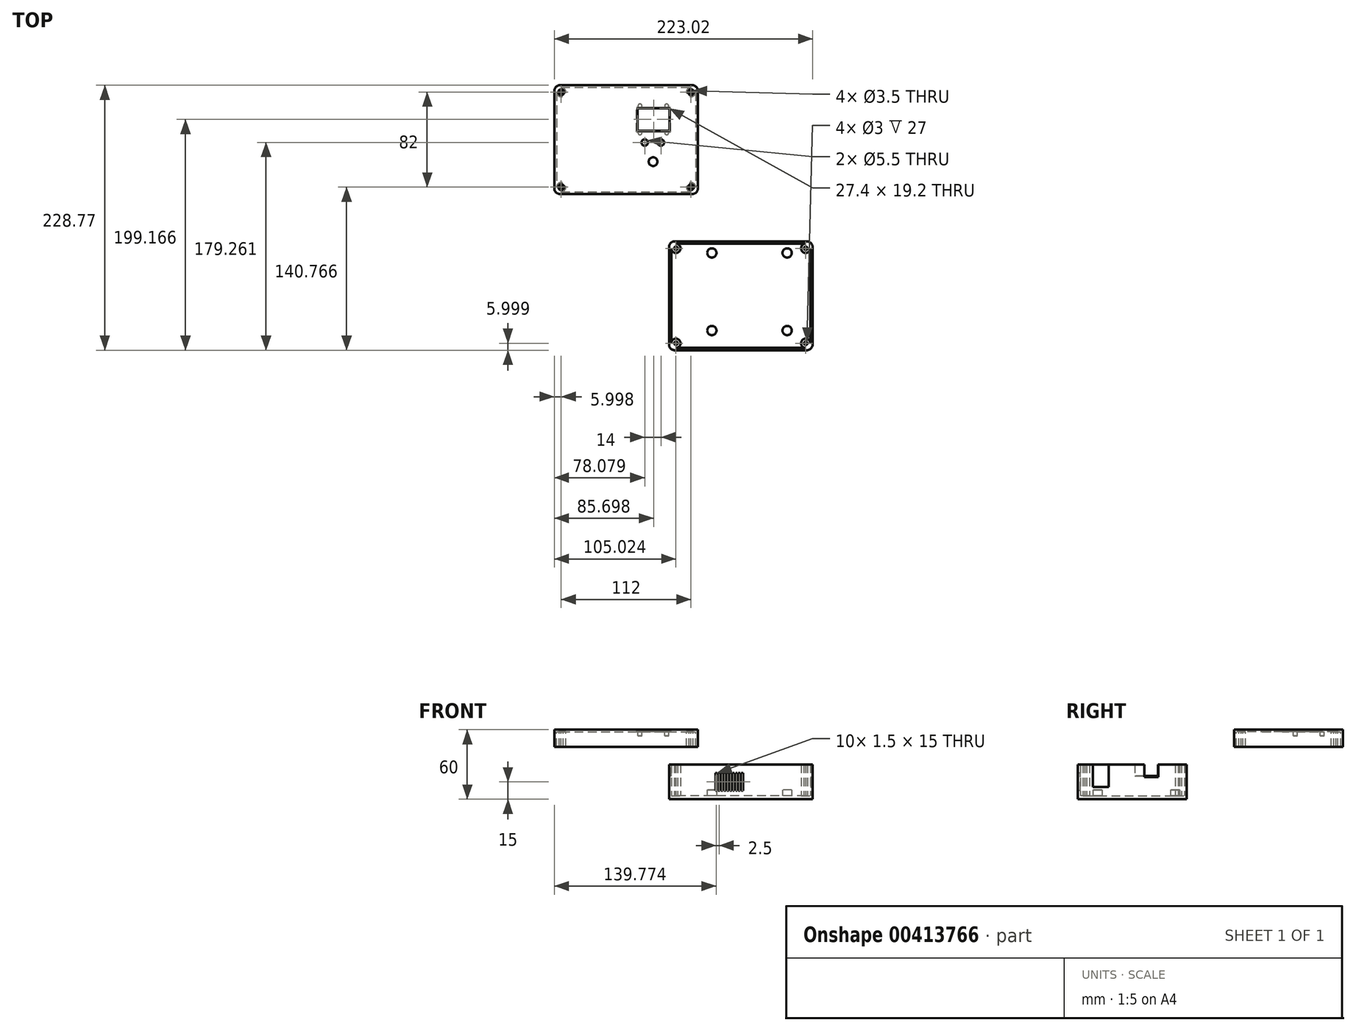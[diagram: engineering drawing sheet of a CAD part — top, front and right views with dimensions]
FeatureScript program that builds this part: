
annotation { "Feature Type Name" : "Feature", "Feature Type Description" : "" }
export const myFeature = defineFeature(function(context is Context, id is Id, definition is map)
    precondition{}
    {
        {
            var Q0;
            Q0=qCreatedBy(makeId("Top.planeOp"),FACE);
            var sketch = newSketch(context, id + "F0", { "sketchPlane" : qUnion([Q0])});
            skLineSegment(sketch, "E0.bottom", {"start": v(-58.78, 54.64) * mm, "end": v(53.22, 54.64) * mm});
            skLineSegment(sketch, "E0.top", {"start": v(-58.78, -35.36) * mm, "end": v(53.22, -35.36) * mm});
            skLineSegment(sketch, "E0.left", {"start": v(-62.78, 50.64) * mm, "end": v(-62.78, -31.36) * mm});
            skLineSegment(sketch, "E0.right", {"start": v(57.22, 50.64) * mm, "end": v(57.22, -31.36) * mm});
            skCircle(sketch, "E1", {"center": v(-58.78, 50.64) * mm, "radius": 4 * mm});
            skCircle(sketch, "E2", {"center": v(53.22, 50.64) * mm, "radius": 4 * mm});
            skCircle(sketch, "E3", {"center": v(-58.78, -31.36) * mm, "radius": 4 * mm});
            skCircle(sketch, "E4", {"center": v(53.22, -31.36) * mm, "radius": 4 * mm});
            skCircle(sketch, "E5", {"center": v(-58.78, 50.64) * mm, "radius": 1.5 * mm});
            skCircle(sketch, "E6", {"center": v(-58.78, -31.36) * mm, "radius": 1.5 * mm});
            skCircle(sketch, "E7", {"center": v(53.22, -31.36) * mm, "radius": 1.5 * mm});
            skCircle(sketch, "E8", {"center": v(53.22, 50.64) * mm, "radius": 1.5 * mm});
            skLineSegment(sketch, "E9.0", {"start": v(-64.78, 56.64) * mm, "end": v(59.22, 56.64) * mm});
            skLineSegment(sketch, "E9.1", {"start": v(-64.78, 56.64) * mm, "end": v(-64.78, -37.36) * mm});
            skLineSegment(sketch, "E9.2", {"start": v(-64.78, -37.36) * mm, "end": v(59.22, -37.36) * mm});
            skLineSegment(sketch, "E9.3", {"start": v(59.22, 56.64) * mm, "end": v(59.22, -37.36) * mm});
            skPoint(sketch, "E10.visualSharp", {"position": v(-62.78, 54.64) * mm});
            skArc(sketch, "E10.filletArc", {"start": v(-58.78, 54.64) * mm, "mid": v(-61.6, 53.47) * mm, "end": v(-62.78, 50.64) * mm});
            skPoint(sketch, "E11.visualSharp", {"position": v(57.22, 54.64) * mm});
            skArc(sketch, "E11.filletArc", {"start": v(57.22, 50.64) * mm, "mid": v(56.05, 53.47) * mm, "end": v(53.22, 54.64) * mm});
            skPoint(sketch, "E12.visualSharp", {"position": v(57.22, -35.36) * mm});
            skArc(sketch, "E12.filletArc", {"start": v(53.22, -35.36) * mm, "mid": v(56.05, -34.19) * mm, "end": v(57.22, -31.36) * mm});
            skPoint(sketch, "E13.visualSharp", {"position": v(-62.78, -35.36) * mm});
            skArc(sketch, "E13.filletArc", {"start": v(-62.78, -31.36) * mm, "mid": v(-61.6, -34.19) * mm, "end": v(-58.78, -35.36) * mm});
            skSolve(sketch);
        }
        {
            var Q0;
            Q0=makeQuery(id+"F0.imprint","IMPRINT",FACE,{"disambiguationData":[TD([[makeQuery(id+"F0.imprint","IMPRINT",EDGE,{"derivedFrom":sQuery(id+"F0.wireOp",EDGE,"E5")}),-1.0]])]});
            var Q1;
            Q1=makeQuery(id+"F0.imprint","IMPRINT",FACE,{"disambiguationData":[TD([[makeQuery(id+"F0.imprint","IMPRINT",EDGE,{"derivedFrom":sQuery(id+"F0.wireOp",EDGE,"E7")}),-1.0]])]});
            var Q2;
            Q2=makeQuery(id+"F0.imprint","IMPRINT",FACE,{"disambiguationData":[TD([[makeQuery(id+"F0.imprint","IMPRINT",EDGE,{"derivedFrom":sQuery(id+"F0.wireOp",EDGE,"E8")}),-1.0]])]});
            var Q3;
            Q3=makeQuery(id+"F0.imprint","IMPRINT",FACE,{"disambiguationData":[TD([[makeQuery(id+"F0.imprint","IMPRINT",EDGE,{"derivedFrom":sQuery(id+"F0.wireOp",EDGE,"E6")}),-1.0]])]});
            var Q4;
            {var subQ3=sQuery(id+"F0.wireOp",EDGE,"E0.bottom");Q4=makeQuery(id+"F0.imprint","IMPRINT",FACE,{"disambiguationData":[TD([[makeQuery(id+"F0.imprint","IMPRINT",EDGE,{"derivedFrom":subQ3}),-1.0]])]});}
            var Q5;
            {var subQ4=sQuery(id+"F0.wireOp",EDGE,"E0.bottom");Q5=makeQuery(id+"F0.imprint","IMPRINT",FACE,{"disambiguationData":[TD([[makeQuery(id+"F0.imprint","IMPRINT",EDGE,{"derivedFrom":subQ4}),1.0]])]});}
            var Q6;
            Q6=makeQuery(id+"F0.imprint","IMPRINT",FACE,{"disambiguationData":[TD([[makeQuery(id+"F0.imprint","IMPRINT",EDGE,{"derivedFrom":sQuery(id+"F0.wireOp",EDGE,"E7")}),1.0]])]});
            var Q7;
            Q7=makeQuery(id+"F0.imprint","IMPRINT",FACE,{"disambiguationData":[TD([[makeQuery(id+"F0.imprint","IMPRINT",EDGE,{"derivedFrom":sQuery(id+"F0.wireOp",EDGE,"E5")}),1.0]])]});
            var Q8;
            Q8=makeQuery(id+"F0.imprint","IMPRINT",FACE,{"disambiguationData":[TD([[makeQuery(id+"F0.imprint","IMPRINT",EDGE,{"derivedFrom":sQuery(id+"F0.wireOp",EDGE,"E8")}),1.0]])]});
            var Q9;
            Q9=makeQuery(id+"F0.imprint","IMPRINT",FACE,{"disambiguationData":[TD([[makeQuery(id+"F0.imprint","IMPRINT",EDGE,{"derivedFrom":sQuery(id+"F0.wireOp",EDGE,"E6")}),1.0]])]});
            extrude(context, id + "F1", {"entities" : qUnion([Q0, Q1, Q2, Q3, Q4, Q5, Q6, Q7, Q8, Q9]), "offsetDistance" : 25 * mm, "depth" : 3 * mm});
        }
        {
            var Q0;
            Q0=makeQuery(id+"F0.imprint","IMPRINT",FACE,{"disambiguationData":[TD([[makeQuery(id+"F0.imprint","IMPRINT",EDGE,{"derivedFrom":sQuery(id+"F0.wireOp",EDGE,"E5")}),-1.0]])]});
            var Q1;
            Q1=makeQuery(id+"F0.imprint","IMPRINT",FACE,{"disambiguationData":[TD([[makeQuery(id+"F0.imprint","IMPRINT",EDGE,{"derivedFrom":sQuery(id+"F0.wireOp",EDGE,"E8")}),-1.0]])]});
            var Q2;
            Q2=makeQuery(id+"F0.imprint","IMPRINT",FACE,{"disambiguationData":[TD([[makeQuery(id+"F0.imprint","IMPRINT",EDGE,{"derivedFrom":sQuery(id+"F0.wireOp",EDGE,"E7")}),-1.0]])]});
            var Q3;
            Q3=makeQuery(id+"F0.imprint","IMPRINT",FACE,{"disambiguationData":[TD([[makeQuery(id+"F0.imprint","IMPRINT",EDGE,{"derivedFrom":sQuery(id+"F0.wireOp",EDGE,"E6")}),-1.0]])]});
            var Q4;
            {var subQ4=sQuery(id+"F0.wireOp",EDGE,"E0.bottom");Q4=makeQuery(id+"F0.imprint","IMPRINT",FACE,{"disambiguationData":[TD([[makeQuery(id+"F0.imprint","IMPRINT",EDGE,{"derivedFrom":subQ4}),1.0]])]});}
            extrude(context, id + "F2", {"entities" : qUnion([Q0, Q1, Q2, Q3, Q4]), "operationType" : NewBodyOperationType.ADD, "depth" : 30 * mm});
        }
        {
            var Q0;
            {var subQ0=sQuery(id+"F0.wireOp",EDGE,"E9.1");var subQ1=sQuery(id+"F0.wireOp",EDGE,"E9.0");Q0=makeQuery(id+"F2.boolean.opBoolean","MERGE",EDGE,{"derivedFrom":[makeQuery(id+"F1.opExtrude","SWEPT_EDGE",EDGE,{"disambiguationData":[OSD([subQ1,subQ0])]}),makeQuery(id+"F2.opExtrude","SWEPT_EDGE",EDGE,{"disambiguationData":[OSD([subQ1,subQ0])]})]});}
            var Q1;
            {var subQ0=sQuery(id+"F0.wireOp",EDGE,"E9.3");var subQ1=sQuery(id+"F0.wireOp",EDGE,"E9.0");Q1=makeQuery(id+"F2.boolean.opBoolean","MERGE",EDGE,{"derivedFrom":[makeQuery(id+"F1.opExtrude","SWEPT_EDGE",EDGE,{"disambiguationData":[OSD([subQ1,subQ0])]}),makeQuery(id+"F2.opExtrude","SWEPT_EDGE",EDGE,{"disambiguationData":[OSD([subQ1,subQ0])]})]});}
            var Q2;
            {var subQ0=sQuery(id+"F0.wireOp",EDGE,"E9.3");var subQ1=sQuery(id+"F0.wireOp",EDGE,"E9.2");Q2=makeQuery(id+"F2.boolean.opBoolean","MERGE",EDGE,{"derivedFrom":[makeQuery(id+"F1.opExtrude","SWEPT_EDGE",EDGE,{"disambiguationData":[OSD([subQ1,subQ0])]}),makeQuery(id+"F2.opExtrude","SWEPT_EDGE",EDGE,{"disambiguationData":[OSD([subQ1,subQ0])]})]});}
            var Q3;
            {var subQ0=sQuery(id+"F0.wireOp",EDGE,"E9.2");var subQ1=sQuery(id+"F0.wireOp",EDGE,"E9.1");Q3=makeQuery(id+"F2.boolean.opBoolean","MERGE",EDGE,{"derivedFrom":[makeQuery(id+"F1.opExtrude","SWEPT_EDGE",EDGE,{"disambiguationData":[OSD([subQ1,subQ0])]}),makeQuery(id+"F2.opExtrude","SWEPT_EDGE",EDGE,{"disambiguationData":[OSD([subQ1,subQ0])]})]});}
            fillet(context, id + "F3", {"entities" : qUnion([Q0, Q1, Q2, Q3]), "radius" : 5 * mm, "tangentPropagation" : true, "allowEdgeOverflow" : false});
        }
        {
            var Q0;
            Q0=makeQuery(id+"F2.boolean.opBoolean","SPLIT",FACE,{"disambiguationData":[TD([makeQuery(id+"F2.opExtrude","SWEPT_FACE",FACE,{"disambiguationData":[OSD([sQuery(id+"F0.wireOp",EDGE,"E0.bottom")])]})])],"derivedFrom":makeQuery(id+"F1.opExtrude","CAP_FACE",FACE,{"disambiguationData":[OSD([sQuery(id+"F0.wireOp",EDGE,"E9.0"),sQuery(id+"F0.wireOp",EDGE,"E9.1"),sQuery(id+"F0.wireOp",EDGE,"E9.2"),sQuery(id+"F0.wireOp",EDGE,"E9.3")])],"isStart":false})});
            var sketch = newSketch(context, id + "F4", { "sketchPlane" : qUnion([Q0])});
            skCircle(sketch, "E14", {"center": v(-27.78, 46.64) * mm, "radius": 4 * mm});
            skCircle(sketch, "E15", {"center": v(37.22, 46.64) * mm, "radius": 4 * mm});
            skCircle(sketch, "E16", {"center": v(-27.78, -20.36) * mm, "radius": 4 * mm});
            skCircle(sketch, "E17", {"center": v(37.22, -20.36) * mm, "radius": 4 * mm});
            skSolve(sketch);
        }
        {
            var Q0;
            Q0 = qSketchRegion(id + "F4", true);
            extrude(context, id + "F5", {"entities" : qUnion([Q0]), "operationType" : NewBodyOperationType.ADD, "offsetDistance" : 25 * mm, "depth" : 5 * mm});
        }
        {
            var Q0;
            {var subQ0=sQuery(id+"F0.wireOp",EDGE,"E9.3");Q0=makeQuery(id+"F2.boolean.opBoolean","MERGE",FACE,{"derivedFrom":[makeQuery(id+"F1.opExtrude","SWEPT_FACE",FACE,{"disambiguationData":[OSD([subQ0])]}),makeQuery(id+"F2.opExtrude","SWEPT_FACE",FACE,{"disambiguationData":[OSD([subQ0])]})]});}
            var sketch = newSketch(context, id + "F6", { "sketchPlane" : qUnion([Q0])});
            skLineSegment(sketch, "E18.bottom", {"start": v(-24.36, 30) * mm, "end": v(-10.86, 30) * mm});
            skLineSegment(sketch, "E18.top", {"start": v(-24.36, 10.5) * mm, "end": v(-10.86, 10.5) * mm});
            skLineSegment(sketch, "E18.left", {"start": v(-24.36, 30) * mm, "end": v(-24.36, 10.5) * mm});
            skLineSegment(sketch, "E18.right", {"start": v(-10.86, 30) * mm, "end": v(-10.86, 10.5) * mm});
            skLineSegment(sketch, "E19.bottom", {"start": v(20.14, 30) * mm, "end": v(32.14, 30) * mm});
            skLineSegment(sketch, "E19.top", {"start": v(20.14, 19) * mm, "end": v(32.14, 19) * mm});
            skLineSegment(sketch, "E19.left", {"start": v(20.14, 30) * mm, "end": v(20.14, 19) * mm});
            skLineSegment(sketch, "E19.right", {"start": v(32.14, 30) * mm, "end": v(32.14, 19) * mm});
            skSolve(sketch);
        }
        {
            var Q0;
            Q0 = qSketchRegion(id + "F6", true);
            extrude(context, id + "F7", {"entities" : qUnion([Q0]), "operationType" : NewBodyOperationType.REMOVE, "oppositeDirection" : true, "depth" : 3 * mm});
        }
        {
            var Q0;
            {var subQ0=sQuery(id+"F0.wireOp",EDGE,"E9.1");Q0=makeQuery(id+"F2.boolean.opBoolean","MERGE",FACE,{"derivedFrom":[makeQuery(id+"F1.opExtrude","SWEPT_FACE",FACE,{"disambiguationData":[OSD([subQ0])]}),makeQuery(id+"F2.opExtrude","SWEPT_FACE",FACE,{"disambiguationData":[OSD([subQ0])]})]});}
            var sketch = newSketch(context, id + "F8", { "sketchPlane" : qUnion([Q0])});
            skLineSegment(sketch, "E20.bottom", {"start": v(-31.64, 30) * mm, "end": v(-11.64, 30) * mm});
            skLineSegment(sketch, "E20.top", {"start": v(-31.64, 20) * mm, "end": v(-11.64, 20) * mm});
            skLineSegment(sketch, "E20.left", {"start": v(-31.64, 30) * mm, "end": v(-31.64, 20) * mm});
            skLineSegment(sketch, "E20.right", {"start": v(-11.64, 30) * mm, "end": v(-11.64, 20) * mm});
            skSolve(sketch);
        }
        {
            var Q0;
            Q0=qCreatedBy(makeId("Top.planeOp"),FACE);
            cPlane(context, id + "F9", {"entities" : qUnion([Q0]), "cplaneType" : CPlaneType.OFFSET, "offset" : 60 * mm, "width" : 150 * mm, "height" : 150 * mm});
        }
        {
            var Q0;
            Q0=qCreatedBy(id+"F9.planeOp",FACE);
            var sketch = newSketch(context, id + "F10", { "sketchPlane" : qUnion([Q0])});
            skLineSegment(sketch, "E21.bottom", {"start": v(-157.8, 189.4) * mm, "end": v(-45.8, 189.4) * mm});
            skLineSegment(sketch, "E21.top", {"start": v(-157.8, 99.4) * mm, "end": v(-45.8, 99.4) * mm});
            skLineSegment(sketch, "E21.left", {"start": v(-161.8, 185.4) * mm, "end": v(-161.8, 103.4) * mm});
            skLineSegment(sketch, "E21.right", {"start": v(-41.8, 185.4) * mm, "end": v(-41.8, 103.4) * mm});
            skCircle(sketch, "E22", {"center": v(-157.8, 185.4) * mm, "radius": 4 * mm});
            skCircle(sketch, "E23", {"center": v(-45.8, 185.4) * mm, "radius": 4 * mm});
            skCircle(sketch, "E24", {"center": v(-157.8, 103.4) * mm, "radius": 4 * mm});
            skCircle(sketch, "E25", {"center": v(-45.8, 103.4) * mm, "radius": 4 * mm});
            skCircle(sketch, "E26", {"center": v(-157.8, 185.4) * mm, "radius": 1.5 * mm});
            skCircle(sketch, "E27", {"center": v(-157.8, 103.4) * mm, "radius": 1.5 * mm});
            skCircle(sketch, "E28", {"center": v(-45.8, 103.4) * mm, "radius": 1.5 * mm});
            skCircle(sketch, "E29", {"center": v(-45.8, 185.4) * mm, "radius": 1.5 * mm});
            skLineSegment(sketch, "E30.0", {"start": v(-163.8, 191.4) * mm, "end": v(-39.8, 191.4) * mm});
            skLineSegment(sketch, "E30.1", {"start": v(-163.8, 191.4) * mm, "end": v(-163.8, 97.4) * mm});
            skLineSegment(sketch, "E30.2", {"start": v(-163.8, 97.4) * mm, "end": v(-39.8, 97.4) * mm});
            skLineSegment(sketch, "E30.3", {"start": v(-39.8, 191.4) * mm, "end": v(-39.8, 97.4) * mm});
            skPoint(sketch, "E31.visualSharp", {"position": v(-161.8, 189.4) * mm});
            skArc(sketch, "E31.filletArc", {"start": v(-157.8, 189.4) * mm, "mid": v(-160.63, 188.23) * mm, "end": v(-161.8, 185.4) * mm});
            skPoint(sketch, "E32.visualSharp", {"position": v(-41.8, 189.4) * mm});
            skArc(sketch, "E32.filletArc", {"start": v(-41.8, 185.4) * mm, "mid": v(-42.97, 188.23) * mm, "end": v(-45.8, 189.4) * mm});
            skPoint(sketch, "E33.visualSharp", {"position": v(-41.8, 99.4) * mm});
            skArc(sketch, "E33.filletArc", {"start": v(-45.8, 99.4) * mm, "mid": v(-42.97, 100.58) * mm, "end": v(-41.8, 103.4) * mm});
            skPoint(sketch, "E34.visualSharp", {"position": v(-161.8, 99.4) * mm});
            skArc(sketch, "E34.filletArc", {"start": v(-161.8, 103.4) * mm, "mid": v(-160.63, 100.58) * mm, "end": v(-157.8, 99.4) * mm});
            skSolve(sketch);
        }
        {
            var Q0;
            {var subQ3=sQuery(id+"F10.wireOp",EDGE,"E21.bottom");Q0=makeQuery(id+"F10.imprint","IMPRINT",FACE,{"disambiguationData":[TD([[makeQuery(id+"F10.imprint","IMPRINT",EDGE,{"derivedFrom":subQ3}),-1.0]])]});}
            var Q1;
            {var subQ4=sQuery(id+"F10.wireOp",EDGE,"E21.bottom");Q1=makeQuery(id+"F10.imprint","IMPRINT",FACE,{"disambiguationData":[TD([[makeQuery(id+"F10.imprint","IMPRINT",EDGE,{"derivedFrom":subQ4}),1.0]])]});}
            var Q2;
            Q2=makeQuery(id+"F10.imprint","IMPRINT",FACE,{"disambiguationData":[TD([[makeQuery(id+"F10.imprint","IMPRINT",EDGE,{"derivedFrom":sQuery(id+"F10.wireOp",EDGE,"E26")}),-1.0]])]});
            var Q3;
            Q3=makeQuery(id+"F10.imprint","IMPRINT",FACE,{"disambiguationData":[TD([[makeQuery(id+"F10.imprint","IMPRINT",EDGE,{"derivedFrom":sQuery(id+"F10.wireOp",EDGE,"E29")}),-1.0]])]});
            var Q4;
            Q4=makeQuery(id+"F10.imprint","IMPRINT",FACE,{"disambiguationData":[TD([[makeQuery(id+"F10.imprint","IMPRINT",EDGE,{"derivedFrom":sQuery(id+"F10.wireOp",EDGE,"E28")}),-1.0]])]});
            var Q5;
            Q5=makeQuery(id+"F10.imprint","IMPRINT",FACE,{"disambiguationData":[TD([[makeQuery(id+"F10.imprint","IMPRINT",EDGE,{"derivedFrom":sQuery(id+"F10.wireOp",EDGE,"E27")}),-1.0]])]});
            extrude(context, id + "F11", {"entities" : qUnion([Q0, Q1, Q2, Q3, Q4, Q5]), "oppositeDirection" : true, "depth" : 2 * mm});
        }
        {
            var Q0;
            {var subQ4=sQuery(id+"F10.wireOp",EDGE,"E21.bottom");Q0=makeQuery(id+"F10.imprint","IMPRINT",FACE,{"disambiguationData":[TD([[makeQuery(id+"F10.imprint","IMPRINT",EDGE,{"derivedFrom":subQ4}),1.0]])]});}
            var Q1;
            Q1=makeQuery(id+"F10.imprint","IMPRINT",FACE,{"disambiguationData":[TD([[makeQuery(id+"F10.imprint","IMPRINT",EDGE,{"derivedFrom":sQuery(id+"F10.wireOp",EDGE,"E26")}),-1.0]])]});
            var Q2;
            Q2=makeQuery(id+"F10.imprint","IMPRINT",FACE,{"disambiguationData":[TD([[makeQuery(id+"F10.imprint","IMPRINT",EDGE,{"derivedFrom":sQuery(id+"F10.wireOp",EDGE,"E29")}),-1.0]])]});
            var Q3;
            Q3=makeQuery(id+"F10.imprint","IMPRINT",FACE,{"disambiguationData":[TD([[makeQuery(id+"F10.imprint","IMPRINT",EDGE,{"derivedFrom":sQuery(id+"F10.wireOp",EDGE,"E28")}),-1.0]])]});
            var Q4;
            Q4=makeQuery(id+"F10.imprint","IMPRINT",FACE,{"disambiguationData":[TD([[makeQuery(id+"F10.imprint","IMPRINT",EDGE,{"derivedFrom":sQuery(id+"F10.wireOp",EDGE,"E27")}),-1.0]])]});
            extrude(context, id + "F12", {"entities" : qUnion([Q0, Q1, Q2, Q3, Q4]), "operationType" : NewBodyOperationType.ADD, "oppositeDirection" : true, "depth" : 15 * mm});
        }
        {
            var Q0;
            {var subQ0=sQuery(id+"F10.wireOp",EDGE,"E30.1");var subQ1=sQuery(id+"F10.wireOp",EDGE,"E30.0");Q0=makeQuery(id+"F12.boolean.opBoolean","MERGE",EDGE,{"derivedFrom":[makeQuery(id+"F11.opExtrude","SWEPT_EDGE",EDGE,{"disambiguationData":[OSD([subQ1,subQ0])]}),makeQuery(id+"F12.opExtrude","SWEPT_EDGE",EDGE,{"disambiguationData":[OSD([subQ1,subQ0])]})]});}
            var Q1;
            {var subQ0=sQuery(id+"F10.wireOp",EDGE,"E30.3");var subQ1=sQuery(id+"F10.wireOp",EDGE,"E30.0");Q1=makeQuery(id+"F12.boolean.opBoolean","MERGE",EDGE,{"derivedFrom":[makeQuery(id+"F11.opExtrude","SWEPT_EDGE",EDGE,{"disambiguationData":[OSD([subQ1,subQ0])]}),makeQuery(id+"F12.opExtrude","SWEPT_EDGE",EDGE,{"disambiguationData":[OSD([subQ1,subQ0])]})]});}
            var Q2;
            {var subQ0=sQuery(id+"F10.wireOp",EDGE,"E30.3");var subQ1=sQuery(id+"F10.wireOp",EDGE,"E30.2");Q2=makeQuery(id+"F12.boolean.opBoolean","MERGE",EDGE,{"derivedFrom":[makeQuery(id+"F11.opExtrude","SWEPT_EDGE",EDGE,{"disambiguationData":[OSD([subQ1,subQ0])]}),makeQuery(id+"F12.opExtrude","SWEPT_EDGE",EDGE,{"disambiguationData":[OSD([subQ1,subQ0])]})]});}
            var Q3;
            {var subQ0=sQuery(id+"F10.wireOp",EDGE,"E30.2");var subQ1=sQuery(id+"F10.wireOp",EDGE,"E30.1");Q3=makeQuery(id+"F12.boolean.opBoolean","MERGE",EDGE,{"derivedFrom":[makeQuery(id+"F11.opExtrude","SWEPT_EDGE",EDGE,{"disambiguationData":[OSD([subQ1,subQ0])]}),makeQuery(id+"F12.opExtrude","SWEPT_EDGE",EDGE,{"disambiguationData":[OSD([subQ1,subQ0])]})]});}
            fillet(context, id + "F13", {"entities" : qUnion([Q0, Q1, Q2, Q3]), "radius" : 5 * mm, "tangentPropagation" : true, "allowEdgeOverflow" : false});
        }
        {
            var Q0;
            Q0=makeQuery(id+"F11.opExtrude","CAP_FACE",FACE,{"disambiguationData":[OSD([sQuery(id+"F10.wireOp",EDGE,"E26"),sQuery(id+"F10.wireOp",EDGE,"E27"),sQuery(id+"F10.wireOp",EDGE,"E28"),sQuery(id+"F10.wireOp",EDGE,"E29"),sQuery(id+"F10.wireOp",EDGE,"E30.0"),sQuery(id+"F10.wireOp",EDGE,"E30.1"),sQuery(id+"F10.wireOp",EDGE,"E30.2"),sQuery(id+"F10.wireOp",EDGE,"E30.3")])],"isStart":false});
            var sketch = newSketch(context, id + "F14", { "sketchPlane" : qUnion([Q0])});
            skCircle(sketch, "E35", {"center": v(-66.8, -173.4) * mm, "radius": 1.75 * mm});
            skCircle(sketch, "E36", {"center": v(-89.8, -173.4) * mm, "radius": 1.75 * mm});
            skCircle(sketch, "E37", {"center": v(-89.8, -150.4) * mm, "radius": 1.75 * mm});
            skCircle(sketch, "E38", {"center": v(-66.8, -150.4) * mm, "radius": 1.75 * mm});
            skSolve(sketch);
        }
        {
            var Q0;
            Q0=qCreatedBy(id+"F9.planeOp",FACE);
            var sketch = newSketch(context, id + "F15", { "sketchPlane" : qUnion([Q0])});
            skLineSegment(sketch, "E39.bottom", {"start": v(-91.8, 171.4) * mm, "end": v(-64.4, 171.4) * mm});
            skLineSegment(sketch, "E39.top", {"start": v(-91.8, 152.2) * mm, "end": v(-64.4, 152.2) * mm});
            skLineSegment(sketch, "E39.left", {"start": v(-91.8, 171.4) * mm, "end": v(-91.8, 152.2) * mm});
            skLineSegment(sketch, "E39.right", {"start": v(-64.4, 171.4) * mm, "end": v(-64.4, 152.2) * mm});
            skSolve(sketch);
        }
        {
            var Q0;
            Q0 = qSketchRegion(id + "F15", true);
            extrude(context, id + "F16", {"entities" : qUnion([Q0]), "operationType" : NewBodyOperationType.REMOVE, "oppositeDirection" : true, "offsetDistance" : 25 * mm, "depth" : 2 * mm});
        }
        {
            var Q0;
            Q0=makeQuery(id+"F14.imprint","IMPRINT",FACE,{"disambiguationData":[TD([[makeQuery(id+"F14.imprint","IMPRINT",EDGE,{"derivedFrom":sQuery(id+"F14.wireOp",EDGE,"E36")}),-1.0]])]});
            var sketch = newSketch(context, id + "F17", { "sketchPlane" : qUnion([Q0])});
            skLineSegment(sketch, "E40", {"start": v(-92.8, -141.12) * mm, "end": v(-92.8, -184.54) * mm, "construction": true});
            skLineSegment(sketch, "E41", {"start": v(-103.77, -151.2) * mm, "end": v(-49.87, -151.2) * mm, "construction": true});
            skLineSegment(sketch, "E42", {"start": v(-103.08, -172.4) * mm, "end": v(-49.67, -172.4) * mm, "construction": true});
            skLineSegment(sketch, "E43", {"start": v(-63.4, -142.01) * mm, "end": v(-63.4, -183.55) * mm, "construction": true});
            skLineSegment(sketch, "E44.bottom", {"start": v(-92.8, -151.2) * mm, "end": v(-63.4, -151.2) * mm});
            skLineSegment(sketch, "E44.top", {"start": v(-92.8, -172.4) * mm, "end": v(-63.4, -172.4) * mm});
            skLineSegment(sketch, "E44.left", {"start": v(-92.8, -151.2) * mm, "end": v(-92.8, -172.4) * mm});
            skLineSegment(sketch, "E44.right", {"start": v(-63.4, -151.2) * mm, "end": v(-63.4, -172.4) * mm});
            skSolve(sketch);
        }
        {
            var Q0;
            Q0 = qSketchRegion(id + "F17", true);
            extrude(context, id + "F18", {"entities" : qUnion([Q0]), "operationType" : NewBodyOperationType.REMOVE, "oppositeDirection" : true, "depth" : 1 * mm, "offsetDistance" : 25 * mm});
        }
        {
            var Q0;
            Q0 = qSketchRegion(id + "F14", true);
            extrude(context, id + "F19", {"entities" : qUnion([Q0]), "operationType" : NewBodyOperationType.ADD, "offsetDistance" : 25 * mm, "depth" : 3.3 * mm});
        }
        {
            var Q0;
            {var subQ3=sQuery(id+"F10.wireOp",EDGE,"E21.bottom");Q0=makeQuery(id+"F10.imprint","IMPRINT",FACE,{"disambiguationData":[TD([[makeQuery(id+"F10.imprint","IMPRINT",EDGE,{"derivedFrom":subQ3}),-1.0]])]});}
            var sketch = newSketch(context, id + "F20", { "sketchPlane" : qUnion([Q0])});
            skCircle(sketch, "E45", {"center": v(-78.52, 125.4) * mm, "radius": 3.75 * mm});
            skLineSegment(sketch, "E46", {"start": v(-60.8, 157.02) * mm, "end": v(-60.8, 98.74) * mm, "construction": true});
            skCircle(sketch, "E47", {"center": v(-85.72, 141.9) * mm, "radius": 2.75 * mm});
            skCircle(sketch, "E48", {"center": v(-71.72, 141.9) * mm, "radius": 2.75 * mm});
            skSolve(sketch);
        }
        {
            var Q0;
            Q0 = qSketchRegion(id + "F20", true);
            extrude(context, id + "F21", {"entities" : qUnion([Q0]), "operationType" : NewBodyOperationType.REMOVE, "oppositeDirection" : true, "depth" : 3 * mm});
        }
        {
            var Q0;
            Q0 = qSketchRegion(id + "F8", true);
            extrude(context, id + "F22", {"entities" : qUnion([Q0]), "operationType" : NewBodyOperationType.REMOVE, "oppositeDirection" : true, "depth" : 3 * mm});
        }
        {
            var Q0;
            Q0=sQuery(id+"F10.wireOp",VERTEX,"E31.filletArc.center");
            var Q1;
            Q1=sQuery(id+"F10.wireOp",VERTEX,"E23.center");
            var Q2;
            Q2=sQuery(id+"F10.wireOp",VERTEX,"E28.center");
            var Q3;
            Q3=sQuery(id+"F10.wireOp",VERTEX,"E34.filletArc.center");
            var Q4;
            Q4=makeQuery(id+"F11.opExtrude","SWEPT_BODY",BODY,{"disambiguationData":[OSD([sQuery(id+"F10.wireOp",EDGE,"E26"),sQuery(id+"F10.wireOp",EDGE,"E27"),sQuery(id+"F10.wireOp",EDGE,"E28"),sQuery(id+"F10.wireOp",EDGE,"E29"),sQuery(id+"F10.wireOp",EDGE,"E30.0"),sQuery(id+"F10.wireOp",EDGE,"E30.1"),sQuery(id+"F10.wireOp",EDGE,"E30.2"),sQuery(id+"F10.wireOp",EDGE,"E30.3")])]});
            hole(context, id + "F23", {"style" : HoleStyle.C_SINK, "endStyle" : HoleEndStyle.THROUGH, "holeDiameter" : 3.5 * mm, "cSinkDiameter" : 5 * mm, "cSinkAngle" : 90 * degree, "isTappedThrough" : true, "tappedDepth" : 12 * mm, "tapClearance" : 3, "startFromSketch" : true, "locations" : qUnion([Q0, Q1, Q2, Q3]), "scope" : qUnion([Q4])});
        }
        {
            var Q0;
            {var subQ3=sQuery(id+"F10.wireOp",EDGE,"E21.bottom");Q0=makeQuery(id+"F10.imprint","IMPRINT",FACE,{"disambiguationData":[TD([[makeQuery(id+"F10.imprint","IMPRINT",EDGE,{"derivedFrom":subQ3}),-1.0]])]});}
            var sketch = newSketch(context, id + "F24", { "sketchPlane" : qUnion([Q0])});
            skSolve(sketch);
        }
        {
            var Q0;
            Q0 = qBodyType(qCreatedBy(id + "F24" ,EDGE), BodyType.WIRE);
            var Q1;
            {var subQ0=sQuery(id+"F0.wireOp",EDGE,"E9.2");Q1=makeQuery(id+"F2.boolean.opBoolean","MERGE",FACE,{"derivedFrom":[makeQuery(id+"F1.opExtrude","SWEPT_FACE",FACE,{"disambiguationData":[OSD([subQ0])]}),makeQuery(id+"F2.opExtrude","SWEPT_FACE",FACE,{"disambiguationData":[OSD([subQ0])]})]});}
            cPlane(context, id + "F25", {"entities" : qUnion([Q0, Q1]), "cplaneType" : CPlaneType.OFFSET, "offset" : 0 * mm, "width" : 150 * mm, "height" : 150 * mm});
        }
        {
            var Q0;
            Q0=qCreatedBy(id+"F25.planeOp",FACE);
            var sketch = newSketch(context, id + "F26", { "sketchPlane" : qUnion([Q0])});
            skLineSegment(sketch, "E49.bottom", {"start": v(-24.78, 22.5) * mm, "end": v(-23.28, 22.5) * mm});
            skLineSegment(sketch, "E49.top", {"start": v(-24.78, 7.5) * mm, "end": v(-23.28, 7.5) * mm});
            skLineSegment(sketch, "E49.left", {"start": v(-24.78, 22.5) * mm, "end": v(-24.78, 7.5) * mm});
            skLineSegment(sketch, "E49.right", {"start": v(-23.28, 22.5) * mm, "end": v(-23.28, 7.5) * mm});
            skLineSegment(sketch, "E50.1.0.0", {"start": v(-22.28, 22.5) * mm, "end": v(-22.28, 7.5) * mm});
            skLineSegment(sketch, "E50.1.0.1", {"start": v(-20.78, 22.5) * mm, "end": v(-20.78, 7.5) * mm});
            skLineSegment(sketch, "E50.1.0.2", {"start": v(-22.28, 22.5) * mm, "end": v(-20.78, 22.5) * mm});
            skLineSegment(sketch, "E50.1.0.3", {"start": v(-22.28, 7.5) * mm, "end": v(-20.78, 7.5) * mm});
            skLineSegment(sketch, "E50.2.0.0", {"start": v(-19.78, 22.5) * mm, "end": v(-19.78, 7.5) * mm});
            skLineSegment(sketch, "E50.2.0.1", {"start": v(-18.28, 22.5) * mm, "end": v(-18.28, 7.5) * mm});
            skLineSegment(sketch, "E50.2.0.2", {"start": v(-19.78, 22.5) * mm, "end": v(-18.28, 22.5) * mm});
            skLineSegment(sketch, "E50.2.0.3", {"start": v(-19.78, 7.5) * mm, "end": v(-18.28, 7.5) * mm});
            skLineSegment(sketch, "E50.3.0.0", {"start": v(-17.28, 22.5) * mm, "end": v(-17.28, 7.5) * mm});
            skLineSegment(sketch, "E50.3.0.1", {"start": v(-15.78, 22.5) * mm, "end": v(-15.78, 7.5) * mm});
            skLineSegment(sketch, "E50.3.0.2", {"start": v(-17.28, 22.5) * mm, "end": v(-15.78, 22.5) * mm});
            skLineSegment(sketch, "E50.3.0.3", {"start": v(-17.28, 7.5) * mm, "end": v(-15.78, 7.5) * mm});
            skLineSegment(sketch, "E50.4.0.0", {"start": v(-14.78, 22.5) * mm, "end": v(-14.78, 7.5) * mm});
            skLineSegment(sketch, "E50.4.0.1", {"start": v(-13.28, 22.5) * mm, "end": v(-13.28, 7.5) * mm});
            skLineSegment(sketch, "E50.4.0.2", {"start": v(-14.78, 22.5) * mm, "end": v(-13.28, 22.5) * mm});
            skLineSegment(sketch, "E50.4.0.3", {"start": v(-14.78, 7.5) * mm, "end": v(-13.28, 7.5) * mm});
            skLineSegment(sketch, "E50.5.0.0", {"start": v(-12.28, 22.5) * mm, "end": v(-12.28, 7.5) * mm});
            skLineSegment(sketch, "E50.5.0.1", {"start": v(-10.78, 22.5) * mm, "end": v(-10.78, 7.5) * mm});
            skLineSegment(sketch, "E50.5.0.2", {"start": v(-12.28, 22.5) * mm, "end": v(-10.78, 22.5) * mm});
            skLineSegment(sketch, "E50.5.0.3", {"start": v(-12.28, 7.5) * mm, "end": v(-10.78, 7.5) * mm});
            skLineSegment(sketch, "E50.6.0.0", {"start": v(-9.78, 22.5) * mm, "end": v(-9.78, 7.5) * mm});
            skLineSegment(sketch, "E50.6.0.1", {"start": v(-8.28, 22.5) * mm, "end": v(-8.28, 7.5) * mm});
            skLineSegment(sketch, "E50.6.0.2", {"start": v(-9.78, 22.5) * mm, "end": v(-8.28, 22.5) * mm});
            skLineSegment(sketch, "E50.6.0.3", {"start": v(-9.78, 7.5) * mm, "end": v(-8.28, 7.5) * mm});
            skLineSegment(sketch, "E50.7.0.0", {"start": v(-7.28, 22.5) * mm, "end": v(-7.28, 7.5) * mm});
            skLineSegment(sketch, "E50.7.0.1", {"start": v(-5.78, 22.5) * mm, "end": v(-5.78, 7.5) * mm});
            skLineSegment(sketch, "E50.7.0.2", {"start": v(-7.28, 22.5) * mm, "end": v(-5.78, 22.5) * mm});
            skLineSegment(sketch, "E50.7.0.3", {"start": v(-7.28, 7.5) * mm, "end": v(-5.78, 7.5) * mm});
            skLineSegment(sketch, "E50.8.0.0", {"start": v(-4.78, 22.5) * mm, "end": v(-4.78, 7.5) * mm});
            skLineSegment(sketch, "E50.8.0.1", {"start": v(-3.28, 22.5) * mm, "end": v(-3.28, 7.5) * mm});
            skLineSegment(sketch, "E50.8.0.2", {"start": v(-4.78, 22.5) * mm, "end": v(-3.28, 22.5) * mm});
            skLineSegment(sketch, "E50.8.0.3", {"start": v(-4.78, 7.5) * mm, "end": v(-3.28, 7.5) * mm});
            skLineSegment(sketch, "E50.9.0.0", {"start": v(-2.28, 22.5) * mm, "end": v(-2.28, 7.5) * mm});
            skLineSegment(sketch, "E50.9.0.1", {"start": v(-0.78, 22.5) * mm, "end": v(-0.78, 7.5) * mm});
            skLineSegment(sketch, "E50.9.0.2", {"start": v(-2.28, 22.5) * mm, "end": v(-0.78, 22.5) * mm});
            skLineSegment(sketch, "E50.9.0.3", {"start": v(-2.28, 7.5) * mm, "end": v(-0.78, 7.5) * mm});
            skLineSegment(sketch, "E50.direction1", {"start": v(-24.78, 7.5) * mm, "end": v(-22.28, 7.5) * mm, "construction": true});
            skSolve(sketch);
        }
        {
            var Q0;
            Q0 = qSketchRegion(id + "F26", true);
            extrude(context, id + "F27", {"entities" : qUnion([Q0]), "operationType" : NewBodyOperationType.REMOVE, "oppositeDirection" : true, "depth" : 3 * mm, "offsetDistance" : 25 * mm});
        }
    });
